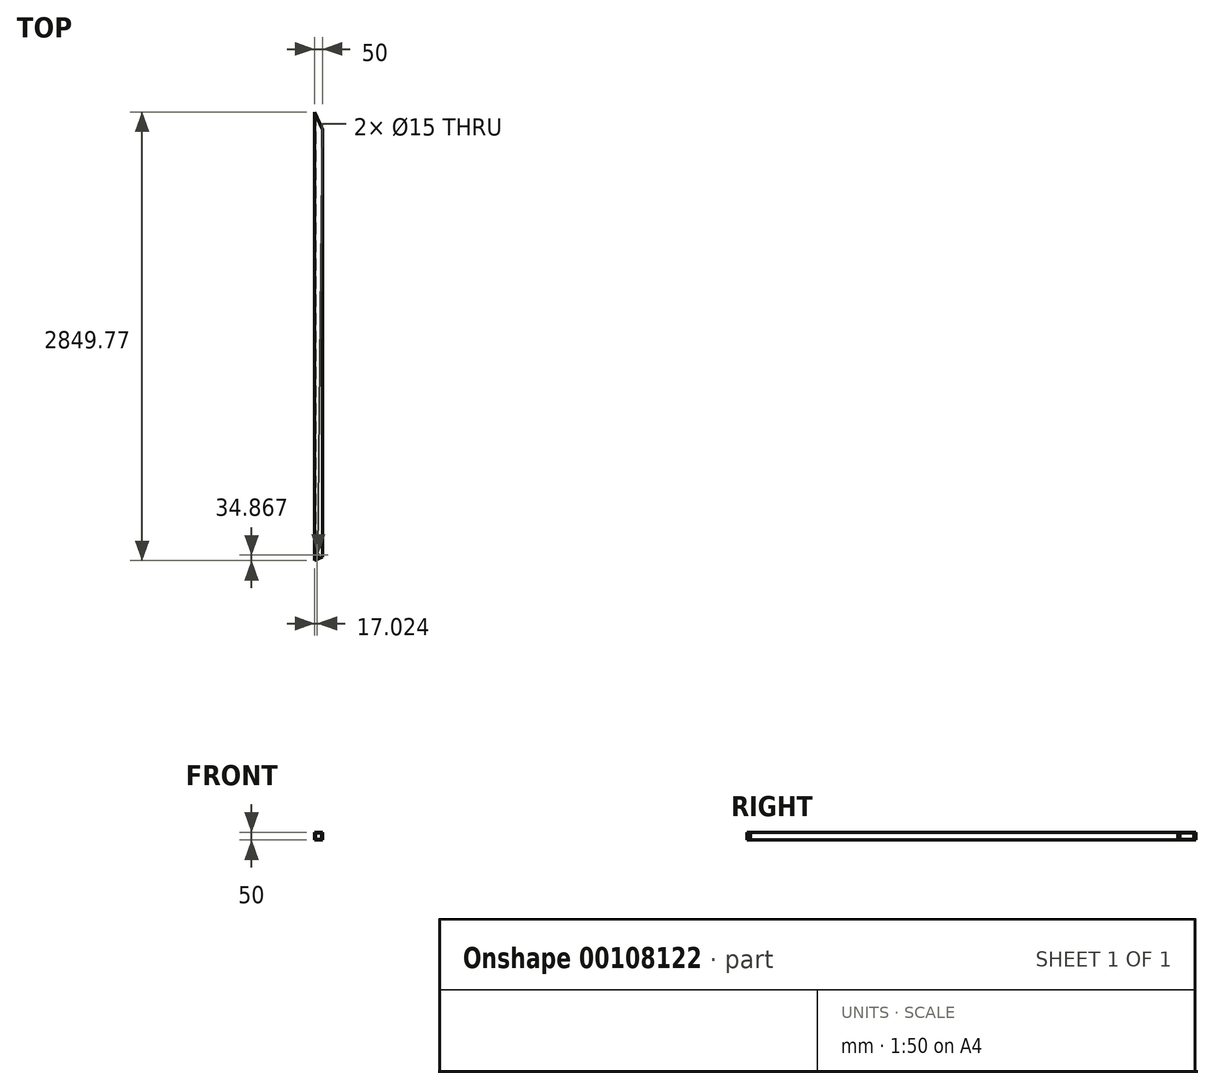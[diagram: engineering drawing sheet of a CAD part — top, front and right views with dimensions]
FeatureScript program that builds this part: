
annotation { "Feature Type Name" : "Feature", "Feature Type Description" : "" }
export const myFeature = defineFeature(function(context is Context, id is Id, definition is map)
    precondition{}
    {
        {
            var Q0;
            Q0=qCreatedBy(makeId("Front.planeOp"),FACE);
            var sketch = newSketch(context, id + "F0", { "sketchPlane" : qUnion([Q0])});
            skLineSegment(sketch, "E0.bottom", {"start": v(25, -25) * mm, "end": v(-25, -25) * mm});
            skLineSegment(sketch, "E0.top", {"start": v(25, 25) * mm, "end": v(-25, 25) * mm});
            skLineSegment(sketch, "E0.left", {"start": v(25, -25) * mm, "end": v(25, 25) * mm});
            skLineSegment(sketch, "E0.right", {"start": v(-25, -25) * mm, "end": v(-25, 25) * mm});
            skPoint(sketch, "E0.middle", {"position": v(0, 0) * mm});
            skLineSegment(sketch, "E1.bottom", {"start": v(20, -20) * mm, "end": v(-20, -20) * mm});
            skLineSegment(sketch, "E1.top", {"start": v(20, 20) * mm, "end": v(-20, 20) * mm});
            skLineSegment(sketch, "E1.left", {"start": v(20, -20) * mm, "end": v(20, 20) * mm});
            skLineSegment(sketch, "E1.right", {"start": v(-20, -20) * mm, "end": v(-20, 20) * mm});
            skSolve(sketch);
        }
        {
            var Q0;
            Q0=makeQuery(id+"F0.imprint","IMPRINT",FACE,{"disambiguationData":[TD([[makeQuery(id+"F0.imprint","IMPRINT",EDGE,{"derivedFrom":sQuery(id+"F0.wireOp",EDGE,"E0.bottom")}),-1.0]])]});
            extrude(context, id + "F1", {"entities" : qUnion([Q0]), "oppositeDirection" : true, "depth" : 3000 * mm});
        }
        {
            var Q0;
            Q0=qCreatedBy(makeId("Top.planeOp"),FACE);
            var sketch = newSketch(context, id + "F2", { "sketchPlane" : qUnion([Q0])});
            skLineSegment(sketch, "E2", {"start": v(-25, 0) * mm, "end": v(2129.3, 952.94) * mm, "construction": true});
            skLineSegment(sketch, "E3", {"start": v(-25, 0) * mm, "end": v(25, 0) * mm});
            skLineSegment(sketch, "E4", {"start": v(25, 0) * mm, "end": v(25, 22.12) * mm});
            skLineSegment(sketch, "E5", {"start": v(25, 22.12) * mm, "end": v(-25, 0) * mm});
            skLineSegment(sketch, "E6", {"start": v(-25, 2911.57) * mm, "end": v(1052.15, 476.47) * mm, "construction": true});
            skLineSegment(sketch, "E7.bottom", {"start": v(185.04, 2498.53) * mm, "end": v(139.32, 2478.3) * mm, "construction": true});
            skLineSegment(sketch, "E7.top", {"start": v(-219.5, 3413.06) * mm, "end": v(-265.22, 3392.83) * mm, "construction": true});
            skLineSegment(sketch, "E7.left", {"start": v(185.04, 2498.53) * mm, "end": v(-219.5, 3413.06) * mm, "construction": true});
            skLineSegment(sketch, "E7.right", {"start": v(139.32, 2478.3) * mm, "end": v(-265.22, 3392.83) * mm, "construction": true});
            skLineSegment(sketch, "E8.bottom", {"start": v(359.98, 2303.44) * mm, "end": v(220.08, 2357.53) * mm, "construction": true});
            skLineSegment(sketch, "E8.top", {"start": v(305.9, 2163.53) * mm, "end": v(165.98, 2217.63) * mm, "construction": true});
            skLineSegment(sketch, "E8.left", {"start": v(359.98, 2303.44) * mm, "end": v(305.9, 2163.53) * mm, "construction": true});
            skLineSegment(sketch, "E8.right", {"start": v(220.08, 2357.53) * mm, "end": v(165.98, 2217.63) * mm, "construction": true});
            skPoint(sketch, "E8.middle", {"position": v(262.98, 2260.53) * mm});
            skLineSegment(sketch, "E9", {"start": v(-25, 2460.3) * mm, "end": v(141.95, 2534.15) * mm, "construction": true});
            skLineSegment(sketch, "E10", {"start": v(141.95, 2534.15) * mm, "end": v(162.18, 2488.42) * mm, "construction": true});
            skLineSegment(sketch, "E11", {"start": v(162.18, 2488.42) * mm, "end": v(-25, 2405.62) * mm, "construction": true});
            skLineSegment(sketch, "E12", {"start": v(-25, 2405.62) * mm, "end": v(-25, 2460.3) * mm, "construction": true});
            skLineSegment(sketch, "E13", {"start": v(-25, 2460.3) * mm, "end": v(25, 2482.41) * mm});
            skLineSegment(sketch, "E14", {"start": v(-25, 2405.62) * mm, "end": v(25, 2427.74) * mm});
            skPoint(sketch, "E15", {"position": v(0, 2471.36) * mm});
            skPoint(sketch, "E16", {"position": v(0, 2416.68) * mm});
            skLineSegment(sketch, "E17", {"start": v(0, 2416.68) * mm, "end": v(0, 2471.36) * mm, "construction": true});
            skPoint(sketch, "E18", {"position": v(0, 2444.02) * mm});
            skLineSegment(sketch, "E19", {"start": v(-25, 2849.77) * mm, "end": v(25, 2736.74) * mm});
            skLineSegment(sketch, "E20", {"start": v(25, 2736.74) * mm, "end": v(25, 3000) * mm});
            skLineSegment(sketch, "E21", {"start": v(25, 3000) * mm, "end": v(-25, 3000) * mm});
            skLineSegment(sketch, "E22", {"start": v(-25, 3000) * mm, "end": v(-25, 2849.77) * mm});
            skLineSegment(sketch, "E23", {"start": v(938.88, 732.54) * mm, "end": v(-250, 206.64) * mm, "construction": true});
            skCircle(sketch, "E24", {"center": v(938.88, 732.54) * mm, "radius": 225 * mm, "construction": true});
            skCircle(sketch, "E25", {"center": v(344.44, 469.59) * mm, "radius": 225 * mm, "construction": true});
            skCircle(sketch, "E26", {"center": v(-250, 206.64) * mm, "radius": 225 * mm, "construction": true});
            skLineSegment(sketch, "E27", {"start": v(-25, 0) * mm, "end": v(2197.3, 983.01) * mm, "construction": true});
            skSolve(sketch);
        }
        {
            var Q0;
            Q0=makeQuery(id+"F2.imprint","IMPRINT",FACE,{"disambiguationData":[TD([[makeQuery(id+"F2.imprint","IMPRINT",EDGE,{"derivedFrom":sQuery(id+"F2.wireOp",EDGE,"E19")}),1.0]])]});
            var Q1;
            Q1=makeQuery(id+"F2.imprint","IMPRINT",FACE,{"disambiguationData":[TD([[makeQuery(id+"F2.imprint","IMPRINT",EDGE,{"derivedFrom":sQuery(id+"F2.wireOp",EDGE,"E3")}),1.0]])]});
            extrude(context, id + "F3", {"entities" : qUnion([Q0, Q1]), "operationType" : NewBodyOperationType.REMOVE, "endBound" : BoundingType.THROUGH_ALL, "oppositeDirection" : true, "depth" : 25 * mm, "hasSecondDirection" : true, "secondDirectionBound" : SecondDirectionBoundingType.THROUGH_ALL, "secondDirectionOppositeDirection" : false, "secondDirectionDepth" : 25 * mm});
        }
        {
            var Q0;
            Q0=makeQuery(id+"F1.opExtrude","SWEPT_FACE",FACE,{"disambiguationData":[OSD([sQuery(id+"F0.wireOp",EDGE,"E0.top")])]});
            var sketch = newSketch(context, id + "F4", { "sketchPlane" : qUnion([Q0])});
            skCircle(sketch, "E28", {"center": v(-7.98, 34.87) * mm, "radius": 7.5 * mm});
            skLineSegment(sketch, "E29", {"start": v(25, 22.12) * mm, "end": v(9.15, 57.95) * mm, "construction": true});
            skSolve(sketch);
        }
        {
            var Q0;
            Q0=makeQuery(id+"F4.imprint","IMPRINT",FACE,{"disambiguationData":[TD([[makeQuery(id+"F4.imprint","IMPRINT",EDGE,{"derivedFrom":sQuery(id+"F4.wireOp",EDGE,"E28")}),1.0]])]});
            extrude(context, id + "F5", {"entities" : qUnion([Q0]), "operationType" : NewBodyOperationType.REMOVE, "endBound" : BoundingType.THROUGH_ALL, "oppositeDirection" : true, "depth" : 25 * mm});
        }
    });
